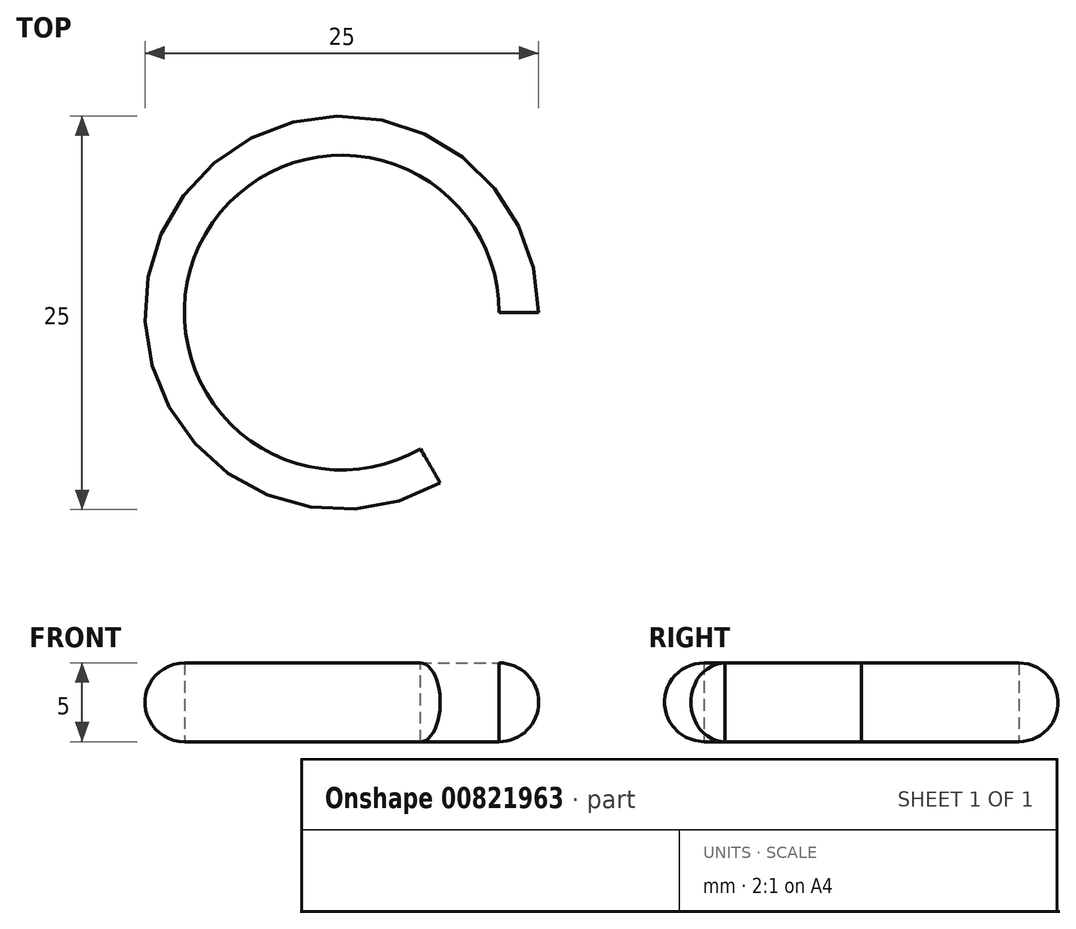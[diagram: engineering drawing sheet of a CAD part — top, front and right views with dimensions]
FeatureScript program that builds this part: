
annotation { "Feature Type Name" : "Feature", "Feature Type Description" : "" }
export const myFeature = defineFeature(function(context is Context, id is Id, definition is map)
    precondition{}
    {
        {
            var Q0;
            Q0=qCreatedBy(makeId("Front.planeOp"),FACE);
            var sketch = newSketch(context, id + "F0", { "sketchPlane" : qUnion([Q0])});
            skLineSegment(sketch, "E0", {"start": v(0, 0) * mm, "end": v(0, 5) * mm});
            skArc(sketch, "E1", {"start": v(0, 0) * mm, "mid": v(2.5, 2.5) * mm, "end": v(0, 5) * mm});
            skLineSegment(sketch, "E2", {"start": v(0, 0) * mm, "end": v(-10, 0) * mm});
            skLineSegment(sketch, "E3", {"start": v(-10, 0) * mm, "end": v(-10, 18.42) * mm});
            skSolve(sketch);
        }
        {
            var Q0;
            Q0=qSketchRegion(id+"F0",true);
            var Q1;
            Q1=sQuery(id+"F0.wireOp",EDGE,"E3");
            revolve(context, id + "F1", {"surfaceOperationType" : NewSurfaceOperationType.NEW, "entities" : qUnion([Q0]), "axis" : qUnion([Q1]), "revolveType" : RevolveType.ONE_DIRECTION, "angle" : 300 * degree});
        }
    });
